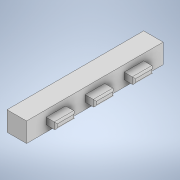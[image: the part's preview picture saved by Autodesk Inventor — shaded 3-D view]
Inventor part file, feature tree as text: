
AUTODESK INVENTOR PART (.ipt)
format: ipt  version: 2020 (Build 240168000, 168)  size: 142,336 bytes
history: native  units: mm
features: extrude x2, sketch x2, fillet x1
ambient origin geometry x8: Origin, YZ Plane, XZ Plane, XY Plane, X Axis, Y Axis, Z Axis, Center Point
bodies: Solid1 (feature_tree)
feature tree (5):
  extrude  "Extrusion1"  Depth=42.0mm
  extrude  "Extrusion2"  TaperAngle=0.0deg  [1 undecoded]
  fillet  "Fillet1"  Radius=6.0mm
  sketch  "Sketch1"  dims[d0=6.0mm d1=42.0mm]
  sketch  "Sketch2"  dims[d2=6.0mm d3=0.0mm d4=6.0mm d5=2.0mm d6=6.0mm d7=30.0mm d9=12.0mm d10=10.0mm d12=10.0mm d14=3.0mm d15=0.0mm d16=0.5mm]
note: 1 required parameter value undecoded (feature->parameter linkage not recoverable at this tier; creation-order binding heuristic only, values carry confidence <= 0.55)
